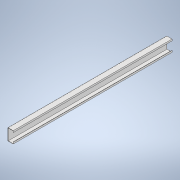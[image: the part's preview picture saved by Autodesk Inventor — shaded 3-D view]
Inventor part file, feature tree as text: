
AUTODESK INVENTOR PART (.ipt)
format: ipt  version: 2020 (Build 240168000, 168)  size: 112,640 bytes
history: native  units: mm
features: extrude x1, sketch x1
ambient origin geometry x8: Origin, YZ Plane, XZ Plane, XY Plane, X Axis, Y Axis, Z Axis, Center Point
bodies: Solid1 (feature_tree)
feature tree (2):
  extrude  "Extrusion1"  Depth=175.0mm
  sketch  "Sketch1"  dims[d0=80.0mm d1=175.0mm d2=25.0mm d3=25.0mm d4=3.5mm d5=2400.0mm d6=0.0mm]
